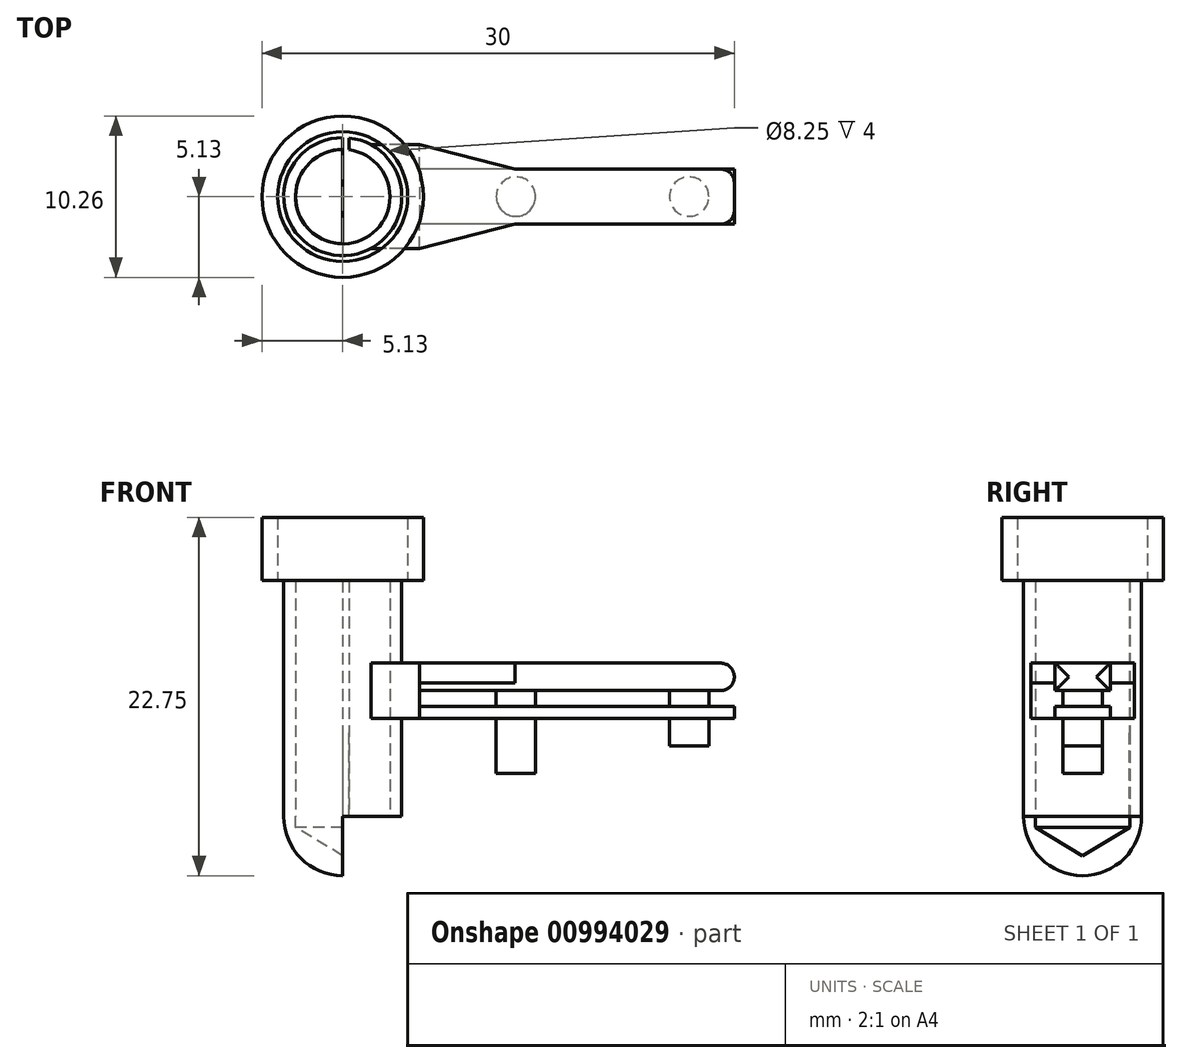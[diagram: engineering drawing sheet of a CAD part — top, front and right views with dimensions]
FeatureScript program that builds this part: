
annotation { "Feature Type Name" : "Feature", "Feature Type Description" : "" }
export const myFeature = defineFeature(function(context is Context, id is Id, definition is map)
    precondition{}
    {
        {
            var Q0;
            Q0=qCreatedBy(makeId("Top.planeOp"),FACE);
            var sketch = newSketch(context, id + "F0", { "sketchPlane" : qUnion([Q0])});
            skCircle(sketch, "E0", {"center": v(0, 0) * mm, "radius": 3 * mm});
            skCircle(sketch, "E1", {"center": v(0, 0) * mm, "radius": 3.75 * mm});
            skLineSegment(sketch, "E2", {"start": v(0, -3.75) * mm, "end": v(0, 3.75) * mm});
            skLineSegment(sketch, "E3.bottom", {"start": v(0, 3.97) * mm, "end": v(0.4, 3.97) * mm});
            skLineSegment(sketch, "E3.top", {"start": v(0, 2.97) * mm, "end": v(0.4, 2.97) * mm});
            skLineSegment(sketch, "E3.left", {"start": v(0, 3.97) * mm, "end": v(0, 2.97) * mm});
            skLineSegment(sketch, "E3.right", {"start": v(0.4, 3.97) * mm, "end": v(0.4, 2.97) * mm});
            skSolve(sketch);
        }
        {
            var Q0;
            {var subQ0=sQuery(id+"F0.wireOp",EDGE,"E2");var subQ1=sQuery(id+"F0.wireOp",EDGE,"E0");var subQ2=makeQuery(id+"F0.imprint","INTERSECT",VERTEX,{"disambiguationData":[OD(0.0)],"derivedFrom":[subQ1,subQ0]});Q0=makeQuery(id+"F0.imprint","IMPRINT",FACE,{"disambiguationData":[TD([[makeQuery(id+"F0.imprint","IMPRINT",EDGE,{"disambiguationData":[TD([[subQ2,-1.0]])],"derivedFrom":subQ1}),-1.0]])]});}
            var Q1;
            {var subQ0=sQuery(id+"F0.wireOp",EDGE,"E2");var subQ1=sQuery(id+"F0.wireOp",EDGE,"E0");var subQ2=makeQuery(id+"F0.imprint","INTERSECT",VERTEX,{"disambiguationData":[OD(0.0)],"derivedFrom":[subQ1,subQ0]});Q1=makeQuery(id+"F0.imprint","IMPRINT",FACE,{"disambiguationData":[TD([[makeQuery(id+"F0.imprint","IMPRINT",EDGE,{"disambiguationData":[TD([[subQ2,1.0]])],"derivedFrom":subQ1}),-1.0]])]});}
            extrude(context, id + "F1", {"entities" : qUnion([Q0, Q1]), "endBound" : BoundingType.SYMMETRIC, "depth" : 15 * mm, "offsetDistance" : 25 * mm});
        }
        {
            var Q0;
            Q0=qCreatedBy(makeId("Top.planeOp"),FACE);
            cPlane(context, id + "F2", {"entities" : qUnion([Q0]), "cplaneType" : CPlaneType.OFFSET, "offset" : 7.5 * mm, "oppositeDirection" : true, "width" : 150 * mm, "height" : 150 * mm});
        }
        {
            var Q0;
            Q0=qCreatedBy(id+"F2.planeOp",FACE);
            var sketch = newSketch(context, id + "F3", { "sketchPlane" : qUnion([Q0])});
            skPoint(sketch, "E4.end.orphan", {"position": v(0, -3.75) * mm});
            skPoint(sketch, "E4.start.orphan", {"position": v(0, 3.75) * mm});
            skLineSegment(sketch, "E5.left", {"start": v(0, -3.75) * mm, "end": v(0, -3.75) * mm});
            skLineSegment(sketch, "E6.right", {"start": v(0, 3.75) * mm, "end": v(0, 3.75) * mm});
            skArc(sketch, "E7", {"start": v(0, 3.75) * mm, "mid": v(-3.75, 0) * mm, "end": v(0, -3.75) * mm});
            skLineSegment(sketch, "E8", {"start": v(0, 3.75) * mm, "end": v(0, -3.75) * mm});
            skSolve(sketch);
        }
        {
            var Q0;
            Q0=qCreatedBy(makeId("Top.planeOp"),FACE);
            var sketch = newSketch(context, id + "F4", { "sketchPlane" : qUnion([Q0])});
            skLineSegment(sketch, "E9.bottom", {"start": v(4.87, -3.3) * mm, "end": v(0, -3.3) * mm});
            skLineSegment(sketch, "E9.top", {"start": v(4.87, 3.3) * mm, "end": v(0, 3.3) * mm});
            skLineSegment(sketch, "E9.left", {"start": v(4.87, -3.3) * mm, "end": v(4.87, 3.3) * mm});
            skPoint(sketch, "E9.middle", {"position": v(0, 0) * mm});
            skLineSegment(sketch, "E10", {"start": v(0, 3.3) * mm, "end": v(0, -3.3) * mm});
            skSolve(sketch);
        }
        {
            var Q0;
            Q0 = qSketchRegion(id + "F4", true);
            extrude(context, id + "F5", {"entities" : qUnion([Q0]), "operationType" : NewBodyOperationType.ADD, "endBound" : BoundingType.SYMMETRIC, "depth" : 2.5 * mm, "offsetDistance" : 25 * mm});
        }
        {
            var Q0;
            Q0=qCreatedBy(makeId("Top.planeOp"),FACE);
            cPlane(context, id + "F6", {"entities" : qUnion([Q0]), "cplaneType" : CPlaneType.OFFSET, "offset" : 2.18 * mm, "oppositeDirection" : true, "width" : 150 * mm, "height" : 150 * mm});
        }
        {
            var Q0;
            Q0=qCreatedBy(id+"F6.planeOp",FACE);
            var sketch = newSketch(context, id + "F7", { "sketchPlane" : qUnion([Q0])});
            skPoint(sketch, "E11", {"position": v(0, 0) * mm});
            skCircle(sketch, "E12", {"center": v(0, 0) * mm, "radius": 15.5 * mm});
            skSolve(sketch);
        }
        {
            var Q0;
            Q0=makeQuery(id+"F5.opExtrude","SWEPT_FACE",FACE,{"disambiguationData":[OSD([sQuery(id+"F4.wireOp",EDGE,"E9.left")])]});
            cPlane(context, id + "F8", {"entities" : qUnion([Q0]), "cplaneType" : CPlaneType.OFFSET, "offset" : 0 * mm, "width" : 150 * mm, "height" : 150 * mm});
        }
        {
            var Q0;
            Q0=qCreatedBy(id+"F8.planeOp",FACE);
            var sketch = newSketch(context, id + "F9", { "sketchPlane" : qUnion([Q0])});
            skLineSegment(sketch, "E13.bottom", {"start": v(1.75, 0.5) * mm, "end": v(-1.75, 0.5) * mm});
            skLineSegment(sketch, "E13.top", {"start": v(1.75, 1.25) * mm, "end": v(-1.75, 1.25) * mm});
            skLineSegment(sketch, "E13.left", {"start": v(1.75, 0.5) * mm, "end": v(1.75, 1.25) * mm});
            skLineSegment(sketch, "E13.right", {"start": v(-1.75, 0.5) * mm, "end": v(-1.75, 1.25) * mm});
            skPoint(sketch, "E13.middle", {"position": v(0, 0.88) * mm});
            skPoint(sketch, "E14.MirrorP", {"position": v(0, -0.88) * mm});
            skLineSegment(sketch, "E15.bottom", {"start": v(1.75, -1.25) * mm, "end": v(-1.75, -1.25) * mm});
            skLineSegment(sketch, "E15.top", {"start": v(1.75, -0.5) * mm, "end": v(-1.75, -0.5) * mm});
            skLineSegment(sketch, "E15.left", {"start": v(1.75, -1.25) * mm, "end": v(1.75, -0.5) * mm});
            skLineSegment(sketch, "E15.right", {"start": v(-1.75, -1.25) * mm, "end": v(-1.75, -0.5) * mm});
            skLineSegment(sketch, "E16", {"start": v(1.75, -0.5) * mm, "end": v(1.75, 0.5) * mm});
            skSolve(sketch);
        }
        {
            var Q0;
            Q0=makeQuery(id+"F9.imprint","IMPRINT",FACE,{"disambiguationData":[TD([[makeQuery(id+"F9.imprint","IMPRINT",EDGE,{"derivedFrom":sQuery(id+"F9.wireOp",EDGE,"E13.bottom")}),-1.0]])]});
            extrude(context, id + "F10", {"entities" : qUnion([Q0]), "operationType" : NewBodyOperationType.ADD, "depth" : 20 * mm, "offsetDistance" : 25 * mm});
        }
        {
            var Q0;
            {var subQ0=sQuery(id+"F4.wireOp",EDGE,"E9.bottom");var subQ1=sQuery(id+"F4.wireOp",EDGE,"E9.top");var subQ2=sQuery(id+"F4.wireOp",EDGE,"E9.left");Q0=makeQuery(id+"F10.boolean.opBoolean","MERGE",FACE,{"derivedFrom":[makeQuery(id+"F5.boolean.opBoolean","SPLIT",FACE,{"disambiguationData":[TD([makeQuery(id+"F1.opExtrude","SWEPT_FACE",FACE,{"disambiguationData":[OSD([sQuery(id+"F0.wireOp",EDGE,"E1")])]})])],"derivedFrom":makeQuery(id+"F5.opExtrude","CAP_FACE",FACE,{"disambiguationData":[OSD([subQ0,subQ1,subQ2,sQuery(id+"F4.wireOp",EDGE,"E10")])],"isStart":false})}),makeQuery(id+"F10.opExtrude","SWEPT_FACE",FACE,{"disambiguationData":[OSD([sQuery(id+"F9.wireOp",EDGE,"E13.top")])]})]});}
            cPlane(context, id + "F11", {"entities" : qUnion([Q0]), "cplaneType" : CPlaneType.OFFSET, "offset" : 0 * mm, "width" : 150 * mm, "height" : 150 * mm});
        }
        {
            var Q0;
            Q0=qCreatedBy(id+"F11.planeOp",FACE);
            var sketch = newSketch(context, id + "F12", { "sketchPlane" : qUnion([Q0])});
            skPoint(sketch, "E17", {"position": v(11, 0) * mm});
            skPoint(sketch, "E18", {"position": v(22, 0) * mm});
            skLineSegment(sketch, "E19", {"start": v(11, 0) * mm, "end": v(22, 0) * mm});
            skLineSegment(sketch, "E20", {"start": v(0, 0) * mm, "end": v(11, 0) * mm});
            skCircle(sketch, "E21", {"center": v(11, 0) * mm, "radius": 1.25 * mm});
            skCircle(sketch, "E22", {"center": v(22, 0) * mm, "radius": 1.25 * mm});
            skSolve(sketch);
        }
        {
            var Q0;
            {var subQ0=sQuery(id+"F4.wireOp",EDGE,"E9.bottom");var subQ1=sQuery(id+"F4.wireOp",EDGE,"E9.top");var subQ2=sQuery(id+"F4.wireOp",EDGE,"E9.left");Q0=makeQuery(id+"F10.boolean.opBoolean","MERGE",FACE,{"derivedFrom":[makeQuery(id+"F5.boolean.opBoolean","SPLIT",FACE,{"disambiguationData":[TD([makeQuery(id+"F1.opExtrude","SWEPT_FACE",FACE,{"disambiguationData":[OSD([sQuery(id+"F0.wireOp",EDGE,"E1")])]})])],"derivedFrom":makeQuery(id+"F5.opExtrude","CAP_FACE",FACE,{"disambiguationData":[OSD([subQ0,subQ1,subQ2,sQuery(id+"F4.wireOp",EDGE,"E10")])],"isStart":false})}),makeQuery(id+"F10.opExtrude","SWEPT_FACE",FACE,{"disambiguationData":[OSD([sQuery(id+"F9.wireOp",EDGE,"E13.top")])]})]});}
            cPlane(context, id + "F13", {"entities" : qUnion([Q0]), "cplaneType" : CPlaneType.OFFSET, "offset" : 0 * mm, "width" : 150 * mm, "height" : 150 * mm});
        }
        {
            var Q0;
            Q0=makeQuery(id+"F9.imprint","IMPRINT",FACE,{"disambiguationData":[TD([[makeQuery(id+"F9.imprint","IMPRINT",EDGE,{"derivedFrom":sQuery(id+"F9.wireOp",EDGE,"E15.bottom")}),-1.0]])]});
            extrude(context, id + "F14", {"entities" : qUnion([Q0]), "depth" : 20 * mm, "offsetDistance" : 25 * mm});
        }
        {
            var Q0;
            Q0=sQuery(id+"F12.wireOp",VERTEX,"E17");
            var Q1;
            Q1=sQuery(id+"F12.wireOp",VERTEX,"E18");
            var Q2;
            Q2=makeQuery(id+"F14.opExtrude","SWEPT_BODY",BODY,{"disambiguationData":[OSD([sQuery(id+"F9.wireOp",EDGE,"E15.bottom"),sQuery(id+"F9.wireOp",EDGE,"E15.top"),sQuery(id+"F9.wireOp",EDGE,"E15.left"),sQuery(id+"F9.wireOp",EDGE,"E15.right")])]});
            hole(context, id + "F15", {"style" : HoleStyle.SIMPLE, "endStyle" : HoleEndStyle.BLIND, "holeDiameter" : 2.5 * mm, "majorDiameter" : 5 * mm, "holeDepth" : 5 * mm, "isTappedThrough" : true, "tappedDepth" : 12 * mm, "tapClearance" : 3, "startFromSketch" : true, "locations" : qUnion([Q0, Q1]), "scope" : qUnion([Q2])});
        }
        {
            var Q0;
            {var subQ0=sQuery(id+"F12.wireOp",EDGE,"E20");var subQ1=sQuery(id+"F12.wireOp",EDGE,"E19");var subQ2=makeQuery(id+"F12.imprint","INTERSECT",VERTEX,{"derivedFrom":[subQ1,subQ0]});Q0=makeQuery(id+"F12.imprint","IMPRINT",FACE,{"disambiguationData":[TD([[makeQuery(id+"F12.imprint","IMPRINT",EDGE,{"disambiguationData":[TD([[subQ2,-1.0]])],"derivedFrom":subQ1}),-1.0]])]});}
            var Q1;
            {var subQ0=sQuery(id+"F12.wireOp",EDGE,"E20");var subQ1=sQuery(id+"F12.wireOp",EDGE,"E19");var subQ2=makeQuery(id+"F12.imprint","INTERSECT",VERTEX,{"derivedFrom":[subQ1,subQ0]});Q1=makeQuery(id+"F12.imprint","IMPRINT",FACE,{"disambiguationData":[TD([[makeQuery(id+"F12.imprint","IMPRINT",EDGE,{"disambiguationData":[TD([[subQ2,-1.0]])],"derivedFrom":subQ1}),1.0]])]});}
            var Q2;
            Q2=sQuery(id+"F12.wireOp",EDGE,"E21");
            var Q3;
            Q3=sQuery(id+"F12.wireOp",EDGE,"E22");
            extrude(context, id + "F16", {"entities" : qUnion([Q0, Q1]), "operationType" : NewBodyOperationType.ADD, "surfaceOperationType" : NewSurfaceOperationType.ADD, "surfaceEntities" : qUnion([Q2, Q3]), "oppositeDirection" : true, "depth" : 6 * mm, "offsetDistance" : 25 * mm});
        }
        {
            var Q0;
            {var subQ0=makeQuery(id+"F1.opExtrude","SWEPT_FACE",FACE,{"disambiguationData":[OSD([sQuery(id+"F0.wireOp",EDGE,"E1")])]});var subQ1=sQuery(id+"F4.wireOp",EDGE,"E9.bottom");var subQ2=sQuery(id+"F4.wireOp",EDGE,"E9.top");var subQ3=sQuery(id+"F4.wireOp",EDGE,"E9.left");Q0=makeQuery(id+"F45tXFDtNHXHnYf_2.splitOp","SPLIT_SURFACE_INTERSECT",FACE,{"derivedFrom":[subQ0,makeQuery(id+"F26.hole-0.boolean.opBoolean","COPY",FACE,{"derivedFrom":makeQuery(id+"F26.hole-0.opRevolve","SWEPT_FACE",FACE,{"disambiguationData":[OSD([sQuery(id+"F26.hole-0.sketch.wireOp",EDGE,"core_line_2")])]})}),makeQuery(id+"F1.opExtrude","SWEPT_FACE",FACE,{"disambiguationData":[OSD([sQuery(id+"F0.wireOp",EDGE,"E0")])]}),makeQuery(id+"F10.boolean.opBoolean","MERGE",FACE,{"derivedFrom":[makeQuery(id+"F5.boolean.opBoolean","SPLIT",FACE,{"disambiguationData":[TD([subQ0])],"derivedFrom":makeQuery(id+"F5.opExtrude","CAP_FACE",FACE,{"disambiguationData":[OSD([subQ1,subQ2,subQ3,sQuery(id+"F4.wireOp",EDGE,"E10")])],"isStart":false})}),makeQuery(id+"F10.opExtrude","SWEPT_FACE",FACE,{"disambiguationData":[OSD([sQuery(id+"F9.wireOp",EDGE,"E13.top")])]})]})],"isFromBackBody":true});}
            var Q1;
            {var subQ0=sQuery(id+"F4.wireOp",EDGE,"E9.bottom");var subQ1=sQuery(id+"F4.wireOp",EDGE,"E9.top");var subQ2=sQuery(id+"F4.wireOp",EDGE,"E9.left");Q1=makeQuery(id+"F10.boolean.opBoolean","MERGE",FACE,{"derivedFrom":[makeQuery(id+"F5.boolean.opBoolean","SPLIT",FACE,{"disambiguationData":[TD([makeQuery(id+"F1.opExtrude","SWEPT_FACE",FACE,{"disambiguationData":[OSD([sQuery(id+"F0.wireOp",EDGE,"E1")])]})])],"derivedFrom":makeQuery(id+"F5.opExtrude","CAP_FACE",FACE,{"disambiguationData":[OSD([subQ0,subQ1,subQ2,sQuery(id+"F4.wireOp",EDGE,"E10")])],"isStart":false})}),makeQuery(id+"F10.opExtrude","SWEPT_FACE",FACE,{"disambiguationData":[OSD([sQuery(id+"F9.wireOp",EDGE,"E13.top")])]})]});}
            extrude(context, id + "F17", {"entities" : qUnion([Q0, Q1]), "operationType" : NewBodyOperationType.ADD, "depth" : 1 * mm, "offsetDistance" : 25 * mm});
        }
        {
            var Q0;
            Q0=makeQuery(id+"F12.imprint","IMPRINT",FACE,{"disambiguationData":[TD([[makeQuery(id+"F12.imprint","IMPRINT",EDGE,{"derivedFrom":sQuery(id+"F12.wireOp",EDGE,"E22")}),1.0]])]});
            extrude(context, id + "F18", {"entities" : qUnion([Q0]), "operationType" : NewBodyOperationType.ADD, "oppositeDirection" : true, "depth" : 4.25 * mm, "offsetDistance" : 25 * mm});
        }
        {
            var Q0;
            Q0=makeQuery(id+"F17.opExtrude","CAP_FACE",FACE,{"disambiguationData":[OSD([sQuery(id+"F0.wireOp",EDGE,"E0"),sQuery(id+"F0.wireOp",EDGE,"E1"),sQuery(id+"F4.wireOp",EDGE,"E9.bottom"),sQuery(id+"F4.wireOp",EDGE,"E9.top"),sQuery(id+"F4.wireOp",EDGE,"E9.left"),sQuery(id+"F4.wireOp",EDGE,"E10"),sQuery(id+"F26.hole-0.sketch.wireOp",EDGE,"core_line_2"),sQuery(id+"F9.wireOp",EDGE,"E13.top")])],"isStart":false});
            var sketch = newSketch(context, id + "F19", { "sketchPlane" : qUnion([Q0])});
            skLineSegment(sketch, "E23", {"start": v(4.87, 3.3) * mm, "end": v(4.87, 1.75) * mm});
            skLineSegment(sketch, "E24", {"start": v(4.87, 1.75) * mm, "end": v(10.95, 1.75) * mm});
            skLineSegment(sketch, "E25", {"start": v(10.95, 1.75) * mm, "end": v(4.87, 3.3) * mm});
            skLineSegment(sketch, "E26", {"start": v(4.87, -3.3) * mm, "end": v(4.87, -1.75) * mm});
            skLineSegment(sketch, "E27", {"start": v(4.87, -1.75) * mm, "end": v(10.95, -1.75) * mm});
            skLineSegment(sketch, "E28", {"start": v(10.95, -1.75) * mm, "end": v(4.87, -3.3) * mm});
            skSolve(sketch);
        }
        {
            var Q0;
            Q0=makeQuery(id+"F19.imprint","IMPRINT",FACE,{"disambiguationData":[TD([[makeQuery(id+"F19.imprint","IMPRINT",EDGE,{"derivedFrom":sQuery(id+"F19.wireOp",EDGE,"E23")}),-1.0]])]});
            var Q1;
            Q1=makeQuery(id+"F19.imprint","IMPRINT",FACE,{"disambiguationData":[TD([[makeQuery(id+"F19.imprint","IMPRINT",EDGE,{"derivedFrom":sQuery(id+"F19.wireOp",EDGE,"E26")}),-1.0]])]});
            extrude(context, id + "F20", {"entities" : qUnion([Q0, Q1]), "operationType" : NewBodyOperationType.ADD, "oppositeDirection" : true, "depth" : 1.25 * mm, "offsetDistance" : 25 * mm});
        }
        {
            var Q0;
            {var subQ0=sQuery(id+"F4.wireOp",EDGE,"E10");var subQ1=sQuery(id+"F4.wireOp",EDGE,"E9.top");Q0=makeQuery(id+"F5.boolean.opBoolean","SPLIT",FACE,{"disambiguationData":[TD([makeQuery(id+"F1.opExtrude","SWEPT_FACE",FACE,{"disambiguationData":[OSD([sQuery(id+"F0.wireOp",EDGE,"E0")])]})])],"derivedFrom":makeQuery(id+"F5.opExtrude","CAP_FACE",FACE,{"disambiguationData":[OSD([sQuery(id+"F4.wireOp",EDGE,"E9.bottom"),subQ1,sQuery(id+"F4.wireOp",EDGE,"E9.left"),subQ0])],"isStart":false})});}
            extrude(context, id + "F21", {"entities" : qUnion([Q0]), "operationType" : NewBodyOperationType.REMOVE, "oppositeDirection" : true, "depth" : 25 * mm, "offsetDistance" : 25 * mm});
        }
        {
            var Q0;
            Q0=makeQuery(id+"F1.opExtrude","CAP_FACE",FACE,{"disambiguationData":[OSD([sQuery(id+"F0.wireOp",EDGE,"E0"),sQuery(id+"F0.wireOp",EDGE,"E1"),sQuery(id+"F0.wireOp",EDGE,"E3.left"),sQuery(id+"F0.wireOp",EDGE,"E3.right")])],"isStart":false});
            var sketch = newSketch(context, id + "F22", { "sketchPlane" : qUnion([Q0])});
            skCircle(sketch, "E29", {"center": v(0, 0) * mm, "radius": 4.12 * mm});
            skCircle(sketch, "E30", {"center": v(0, 0) * mm, "radius": 5.12 * mm});
            skSolve(sketch);
        }
        {
            var Q0;
            Q0=makeQuery(id+"F22.imprint","IMPRINT",FACE,{"disambiguationData":[TD([[makeQuery(id+"F22.imprint","IMPRINT",EDGE,{"derivedFrom":sQuery(id+"F22.wireOp",EDGE,"E29")}),-1.0]])]});
            extrude(context, id + "F23", {"entities" : qUnion([Q0]), "depth" : 4 * mm, "offsetDistance" : 25 * mm});
        }
        {
            var Q0;
            {var subQ0=sQuery(id+"F9.wireOp",EDGE,"E13.top");Q0=makeQuery(id+"F17.boolean.opBoolean","MERGE",FACE,{"derivedFrom":[makeQuery(id+"F10.opExtrude","CAP_FACE",FACE,{"disambiguationData":[OSD([sQuery(id+"F9.wireOp",EDGE,"E13.bottom"),subQ0,sQuery(id+"F9.wireOp",EDGE,"E13.left"),sQuery(id+"F9.wireOp",EDGE,"E13.right")])],"isStart":false}),makeQuery(id+"F17.opExtrude","SWEPT_FACE",FACE,{"disambiguationData":[OSD([subQ0])]})]});}
            fillet(context, id + "F24", {"entities" : qUnion([Q0]), "radius" : 0.88 * mm, "tangentPropagation" : true, "allowEdgeOverflow" : false});
        }
        {
            var Q0;
            Q0=makeQuery(id+"F3.imprint","IMPRINT",FACE,{"disambiguationData":[TD([[makeQuery(id+"F3.imprint","IMPRINT",EDGE,{"derivedFrom":sQuery(id+"F3.wireOp",EDGE,"E7")}),1.0]])]});
            var Q1;
            Q1=sQuery(id+"F3.wireOp",EDGE,"E8");
            revolve(context, id + "F25", {"operationType" : NewBodyOperationType.ADD, "surfaceOperationType" : NewSurfaceOperationType.NEW, "entities" : qUnion([Q0]), "axis" : qUnion([Q1]), "revolveType" : RevolveType.ONE_DIRECTION, "angle" : 90 * degree});
        }
        {
            var Q0;
            Q0=sQuery(id+"F7.wireOp",VERTEX,"E11");
            var Q1;
            Q1=makeQuery(id+"F1.opExtrude","SWEPT_BODY",BODY,{"disambiguationData":[OSD([sQuery(id+"F0.wireOp",EDGE,"E0"),sQuery(id+"F0.wireOp",EDGE,"E1"),sQuery(id+"F0.wireOp",EDGE,"E3.left"),sQuery(id+"F0.wireOp",EDGE,"E3.right")])]});
            hole(context, id + "F26", {"style" : HoleStyle.SIMPLE, "endStyle" : HoleEndStyle.BLIND, "holeDiameter" : 6 * mm, "majorDiameter" : 5 * mm, "holeDepth" : 6 * mm, "isTappedThrough" : true, "tappedDepth" : 12 * mm, "tapClearance" : 3, "startFromSketch" : true, "locations" : qUnion([Q0]), "scope" : qUnion([Q1])});
        }
    });
